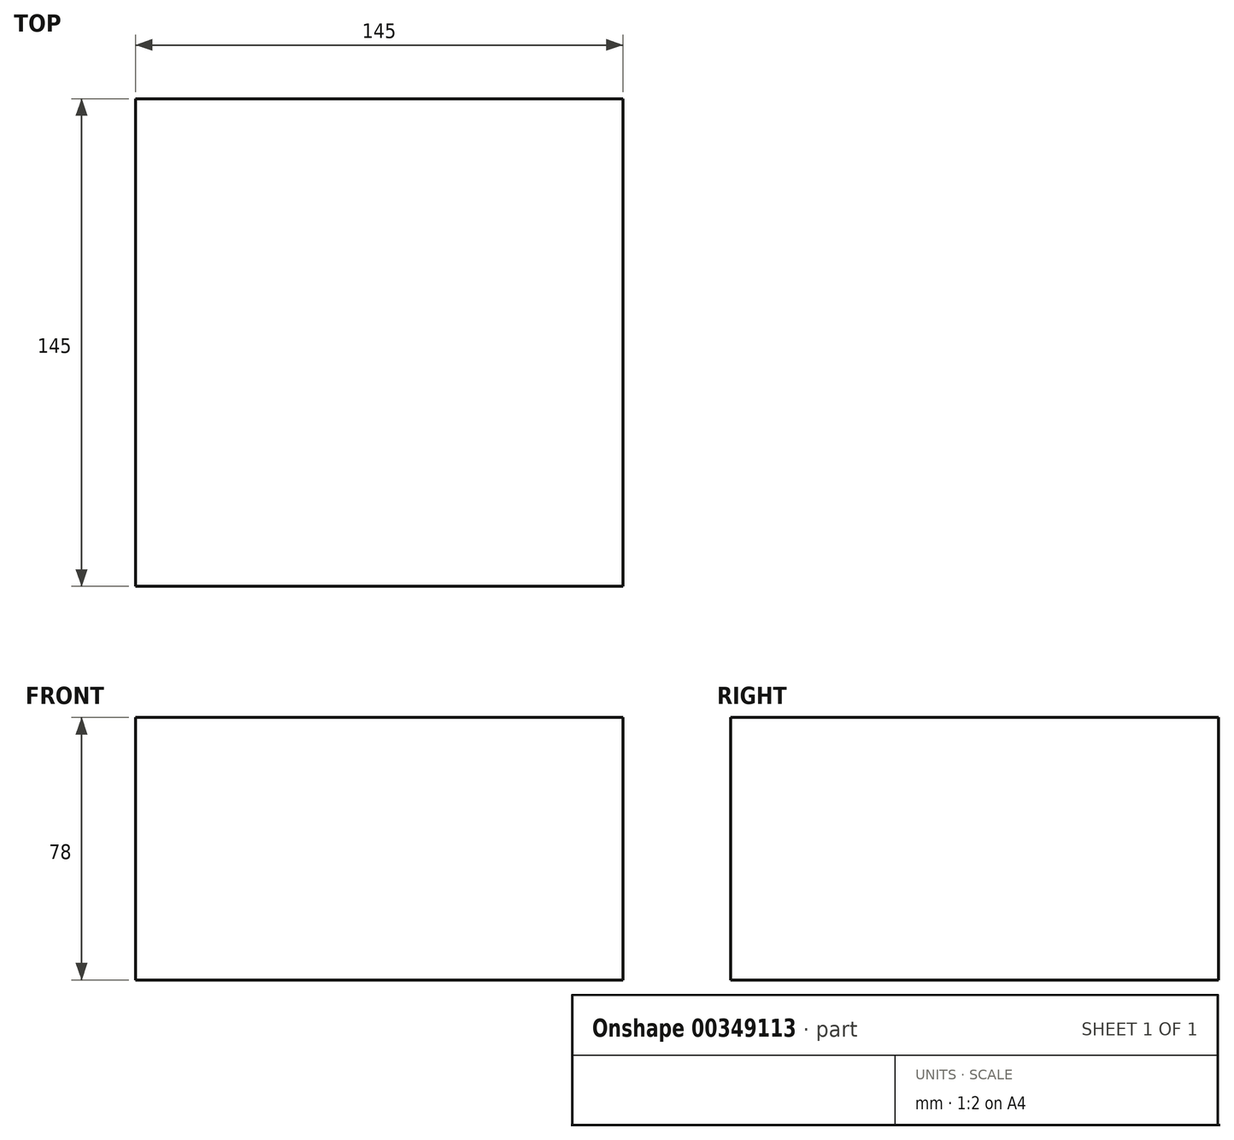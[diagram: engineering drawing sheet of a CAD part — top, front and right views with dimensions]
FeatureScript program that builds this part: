
annotation { "Feature Type Name" : "Feature", "Feature Type Description" : "" }
export const myFeature = defineFeature(function(context is Context, id is Id, definition is map)
    precondition{}
    {
        {
            var Q0;
            Q0=qCreatedBy(makeId("Top.planeOp"),FACE);
            var sketch = newSketch(context, id + "F0", { "sketchPlane" : qUnion([Q0])});
            skLineSegment(sketch, "E0.bottom", {"start": v(-72.5, 72.5) * mm, "end": v(72.5, 72.5) * mm});
            skLineSegment(sketch, "E0.top", {"start": v(-72.5, -72.5) * mm, "end": v(72.5, -72.5) * mm});
            skLineSegment(sketch, "E0.left", {"start": v(-72.5, 72.5) * mm, "end": v(-72.5, -72.5) * mm});
            skLineSegment(sketch, "E0.right", {"start": v(72.5, 72.5) * mm, "end": v(72.5, -72.5) * mm});
            skSolve(sketch);
        }
        {
            var Q0;
            Q0 = qSketchRegion(id + "F0", true);
            extrude(context, id + "F1", {"entities" : qUnion([Q0]), "endBound" : BoundingType.SYMMETRIC, "depth" : 78 * mm});
        }
    });
